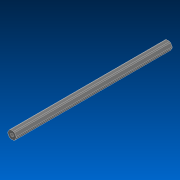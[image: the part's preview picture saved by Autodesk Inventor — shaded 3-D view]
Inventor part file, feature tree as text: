
AUTODESK INVENTOR PART (.ipt)
format: ipt  version: 2022.2 (Build 262287000, 287)  size: 121,856 bytes
history: native  units: in
note: dims shown in document units (in); Inventor stores cm internally (conversion verified against a paired STEP export)
features: extrude x1, sketch x1, other x1
ambient origin geometry x8: Origin, YZ Plane, XZ Plane, XY Plane, X Axis, Y Axis, Z Axis, Center Point
bodies: Solid1 (feature_tree)
feature tree (3):
  extrude  "Extrusion1"  TaperAngle=0.0deg  [1 undecoded]
  sketch  "Sketch1"  dims[d0=26.0in d1=0.0in]
  other  "Cut-Extrude2"
note: 1 required parameter value undecoded (feature->parameter linkage not recoverable at this tier; creation-order binding heuristic only, values carry confidence <= 0.55)
